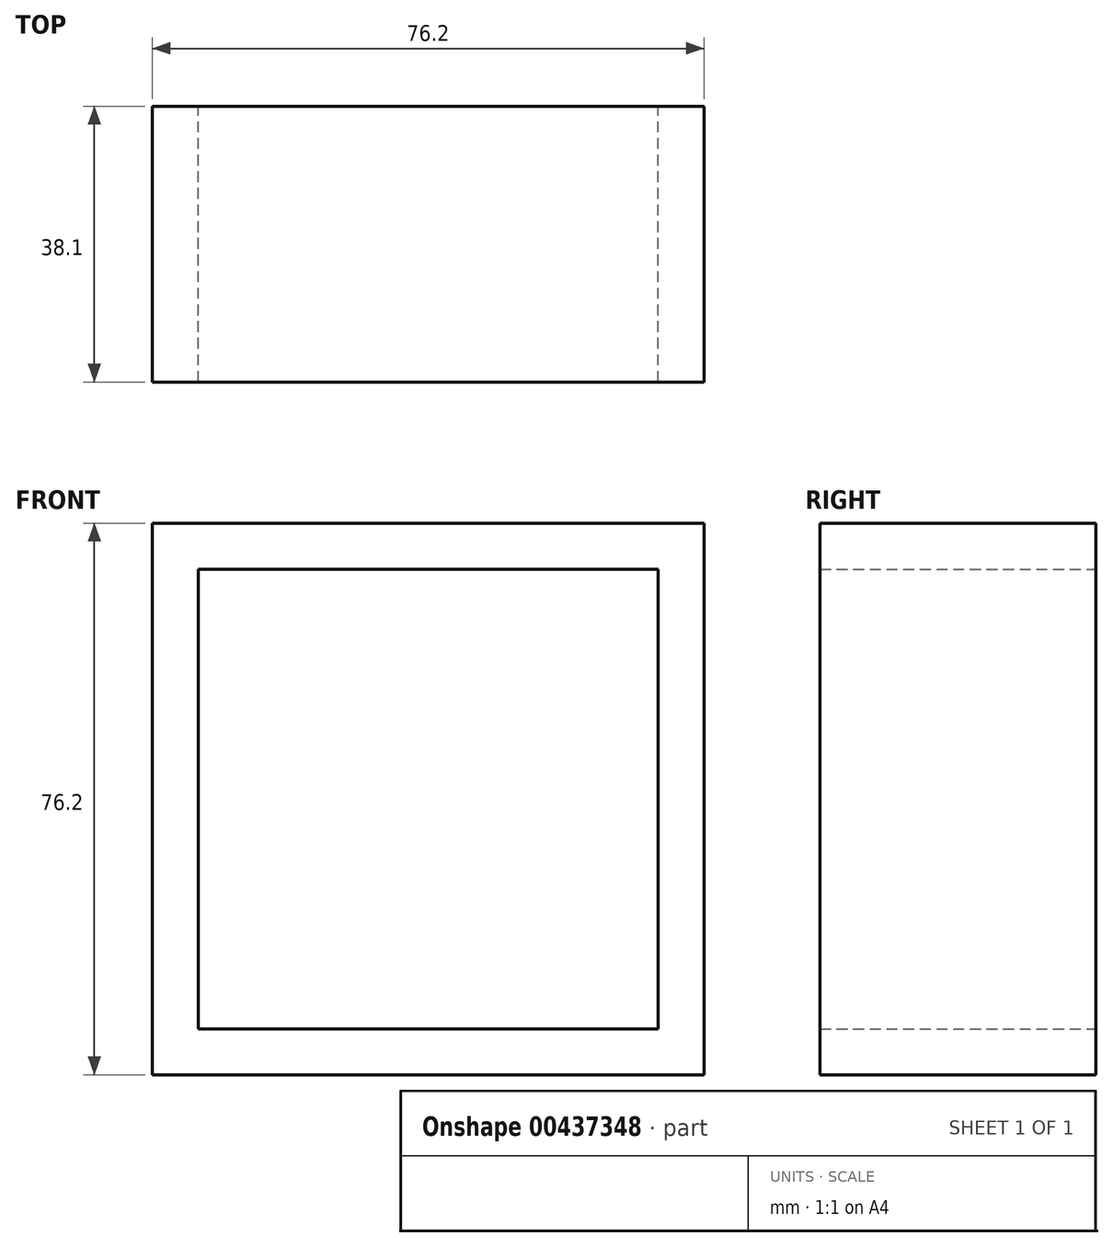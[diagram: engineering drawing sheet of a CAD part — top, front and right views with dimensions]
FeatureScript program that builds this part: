
annotation { "Feature Type Name" : "Feature", "Feature Type Description" : "" }
export const myFeature = defineFeature(function(context is Context, id is Id, definition is map)
    precondition{}
    {
        {
            var Q0;
            Q0=qCreatedBy(makeId("Front.planeOp"),FACE);
            var sketch = newSketch(context, id + "F0", { "sketchPlane" : qUnion([Q0])});
            skLineSegment(sketch, "E0.bottom", {"start": v(38.1, -38.1) * mm, "end": v(-38.1, -38.1) * mm});
            skLineSegment(sketch, "E0.top", {"start": v(38.1, 38.1) * mm, "end": v(-38.1, 38.1) * mm});
            skLineSegment(sketch, "E0.left", {"start": v(38.1, -38.1) * mm, "end": v(38.1, 38.1) * mm});
            skLineSegment(sketch, "E0.right", {"start": v(-38.1, -38.1) * mm, "end": v(-38.1, 38.1) * mm});
            skPoint(sketch, "E0.middle", {"position": v(0, 0) * mm});
            skLineSegment(sketch, "E1.bottom", {"start": v(31.75, -31.75) * mm, "end": v(-31.75, -31.75) * mm});
            skLineSegment(sketch, "E1.top", {"start": v(31.75, 31.75) * mm, "end": v(-31.75, 31.75) * mm});
            skLineSegment(sketch, "E1.left", {"start": v(31.75, -31.75) * mm, "end": v(31.75, 31.75) * mm});
            skLineSegment(sketch, "E1.right", {"start": v(-31.75, -31.75) * mm, "end": v(-31.75, 31.75) * mm});
            skSolve(sketch);
        }
        {
            var Q0;
            Q0 = qSketchRegion(id + "F0", true);
            extrude(context, id + "F1", {"entities" : qUnion([Q0]), "depth" : 38.1 * mm});
        }
    });
